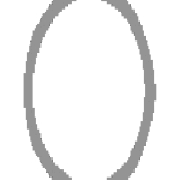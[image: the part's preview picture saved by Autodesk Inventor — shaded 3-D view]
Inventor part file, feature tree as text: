
AUTODESK INVENTOR PART (.ipt)
format: ipt  version: 2021 (Build 250183000, 183)  size: 110,080 bytes
history: native  units: in
note: dims shown in document units (in); Inventor stores cm internally (conversion verified against a paired STEP export)
features: other x4, sketch x3, plane x1
ambient origin geometry x8: Origin, YZ Plane, XZ Plane, XY Plane, X Axis, Y Axis, Z Axis, Center Point
bodies: Solid1 (feature_tree), Body (feature_tree)
feature tree (8):
  other  "Driven Length"
  other  "Frame Generator"
  other  "Start Plane"
  other  "End Plane"
  sketch  "Sketch"  dims[d2=15.5in d4=-0.0in d5=15.5in d6=0.12in d7=0.0in d10=90.0deg d9=15.5in]
  sketch  "Sketch4"  dims[d0=1.0in]
  plane  "Work Plane4"
  sketch  "Sketch5"  dims[d1=0.065in]
